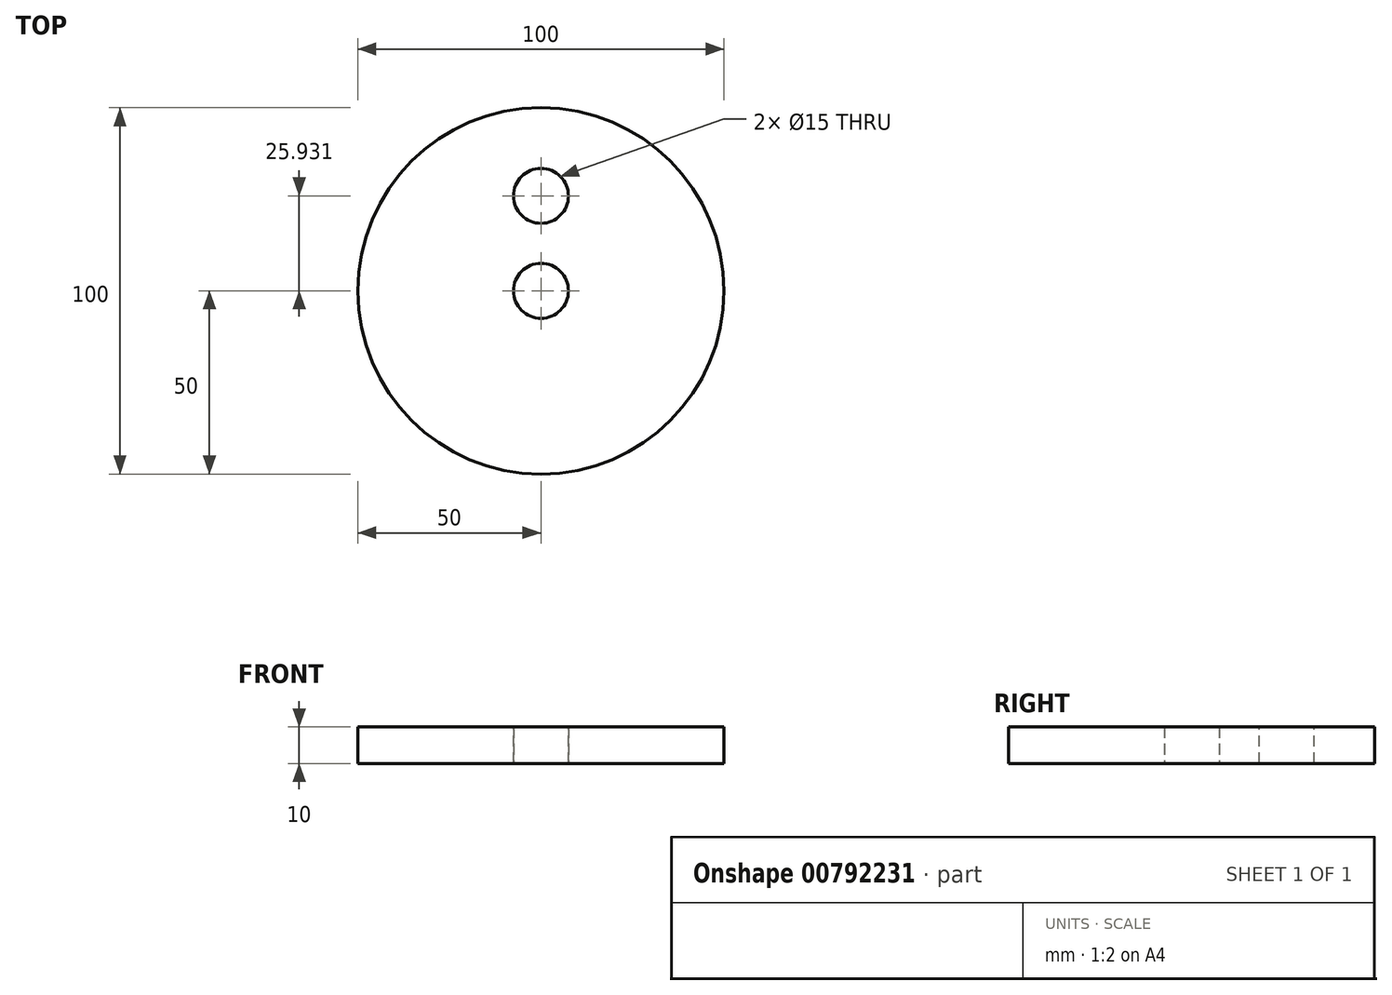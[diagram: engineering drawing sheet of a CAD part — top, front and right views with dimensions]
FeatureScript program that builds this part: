
annotation { "Feature Type Name" : "Feature", "Feature Type Description" : "" }
export const myFeature = defineFeature(function(context is Context, id is Id, definition is map)
    precondition{}
    {
        {
            var Q0;
            Q0=qCreatedBy(makeId("Top.planeOp"),FACE);
            var sketch = newSketch(context, id + "F0", { "sketchPlane" : qUnion([Q0])});
            skCircle(sketch, "E0", {"center": v(0, 0) * mm, "radius": 50 * mm});
            skSolve(sketch);
        }
        {
            var Q0;
            Q0=makeQuery(id+"F0.imprint","IMPRINT",FACE,{"disambiguationData":[TD([[makeQuery(id+"F0.imprint","IMPRINT",EDGE,{"derivedFrom":sQuery(id+"F0.wireOp",EDGE,"E0")}),1.0]])]});
            var sketch = newSketch(context, id + "F1", { "sketchPlane" : qUnion([Q0])});
            skSolve(sketch);
        }
        {
            var Q0;
            Q0=makeQuery(id+"F0.imprint","IMPRINT",FACE,{"disambiguationData":[TD([[makeQuery(id+"F0.imprint","IMPRINT",EDGE,{"derivedFrom":sQuery(id+"F0.wireOp",EDGE,"E0")}),1.0]])]});
            extrude(context, id + "F2", {"entities" : qUnion([Q0]), "depth" : 10 * mm, "offsetDistance" : 25 * mm});
        }
        {
            var Q0;
            Q0=makeQuery(id+"F2.opExtrude","CAP_FACE",FACE,{"disambiguationData":[OSD([sQuery(id+"F0.wireOp",EDGE,"E0")])],"isStart":false});
            var sketch = newSketch(context, id + "F3", { "sketchPlane" : qUnion([Q0])});
            skCircle(sketch, "E1", {"center": v(0, 25.93) * mm, "radius": 5 * mm});
            skSolve(sketch);
        }
        {
            var Q0;
            Q0=sQuery(id+"F3.wireOp",VERTEX,"E1.center");
            var Q1;
            Q1=makeQuery(id+"F2.opExtrude","SWEPT_BODY",BODY,{"disambiguationData":[OSD([sQuery(id+"F0.wireOp",EDGE,"E0")])]});
            hole(context, id + "F4", {"style" : HoleStyle.SIMPLE, "endStyle" : HoleEndStyle.THROUGH, "holeDiameter" : 15 * mm, "majorDiameter" : 5 * mm, "isTappedThrough" : true, "tappedDepth" : 12 * mm, "tapClearance" : 3, "locations" : qUnion([Q0]), "scope" : qUnion([Q1])});
        }
        {
            var Q0;
            Q0=makeQuery(id+"F1.imprint","IMPRINT",FACE,{"disambiguationData":[TD([[makeQuery(id+"F1.imprint","IMPRINT",EDGE,{"derivedFrom":makeQuery(id+"F0.imprint","IMPRINT",EDGE,{"derivedFrom":sQuery(id+"F0.wireOp",EDGE,"E0")})}),1.0]])]});
            var sketch = newSketch(context, id + "F5", { "sketchPlane" : qUnion([Q0])});
            skCircle(sketch, "E2", {"center": v(0, 0) * mm, "radius": 7.5 * mm});
            skSolve(sketch);
        }
        {
            var Q0;
            Q0=sQuery(id+"F5.wireOp",VERTEX,"E2.center");
            var Q1;
            Q1=makeQuery(id+"F2.opExtrude","SWEPT_BODY",BODY,{"disambiguationData":[OSD([sQuery(id+"F0.wireOp",EDGE,"E0")])]});
            hole(context, id + "F6", {"style" : HoleStyle.SIMPLE, "endStyle" : HoleEndStyle.THROUGH, "oppositeDirection" : true, "holeDiameter" : 15 * mm, "majorDiameter" : 5 * mm, "isTappedThrough" : true, "tappedDepth" : 12 * mm, "tapClearance" : 3, "locations" : qUnion([Q0]), "scope" : qUnion([Q1])});
        }
    });
